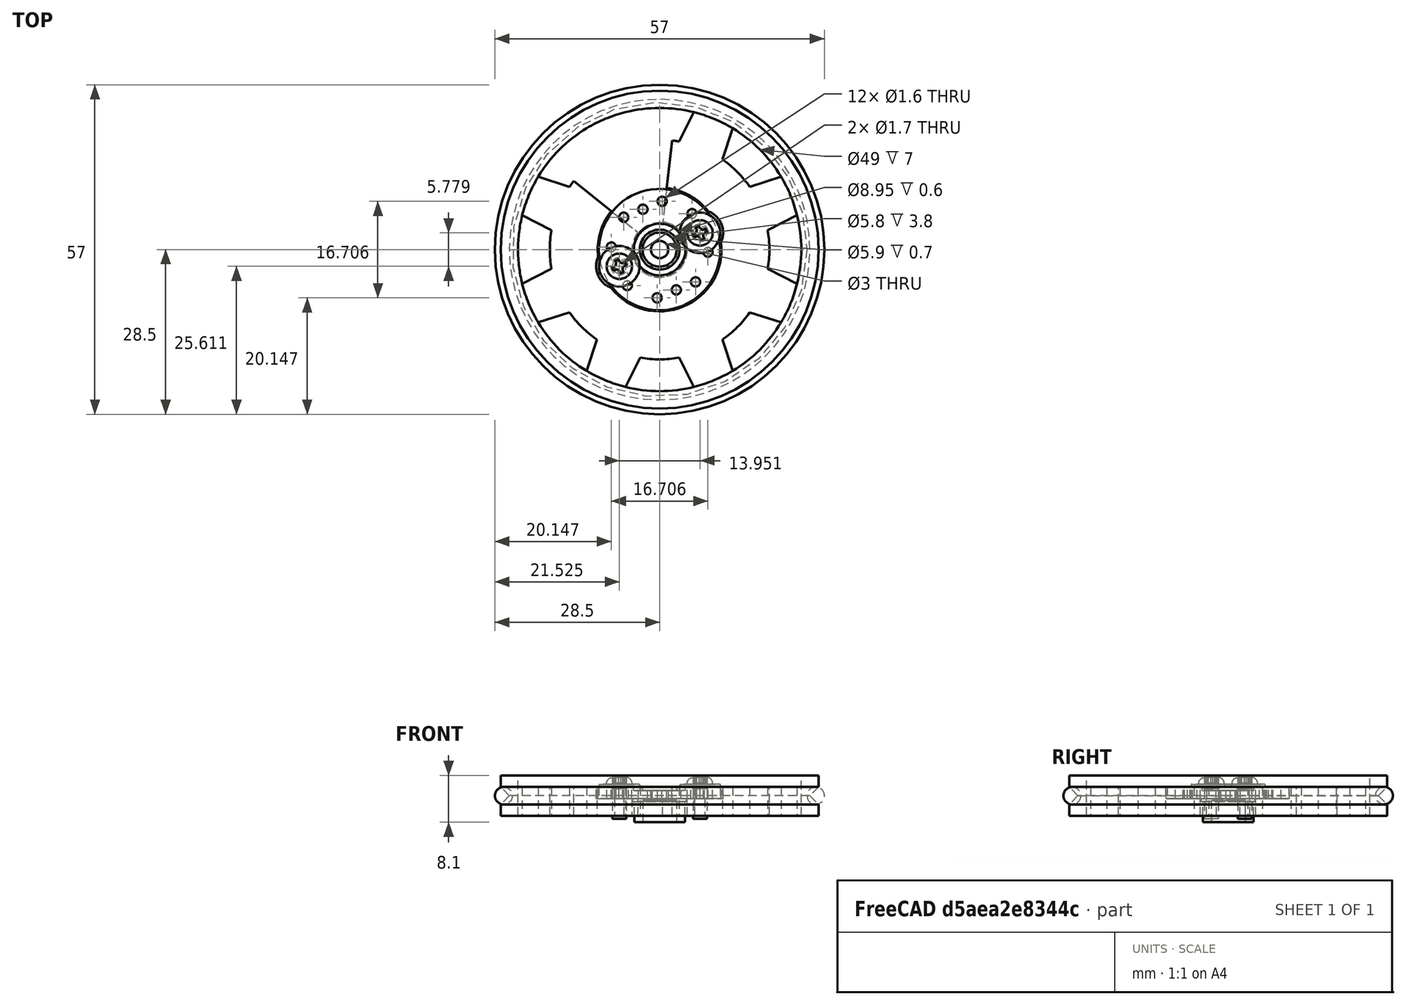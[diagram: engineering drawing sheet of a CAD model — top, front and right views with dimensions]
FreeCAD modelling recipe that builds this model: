
FCSTD DOCUMENT  (FreeCAD 0.14R3702 (Git))
Label: Renacuajo-wheel-open-hardware-assembly
License: CC-BY 3.0
LicenseURL: http://creativecommons.org/licenses/by/3.0/
objects: Part::Feature×4, Part::Torus×1, Part::Compound×1
note: 6 computed .brp shape members not serialized (recipe doc carries the construction recipe); baked Part::Feature solids carry a one-line shape summary decoded from their .brp

FEATURE [Part::Feature] Pocket  label="Renacuajo-open-hardware-wheel"
  Placement = pos=(0,0,0) rot=(1,0,0;1.5708rad)
  shape: bbox 55 x 55 x 7 mm, 43 faces (baked)
FEATURE [Part::Torus] Torus  label="o-ring"
  Angle1 = -180
  Angle2 = 180
  Angle3 = 360
  Radius1 = 27
  Radius2 = 1.5
FEATURE [Part::Feature] Pocket001  label="small-rounded-horn"
  Placement = pos=(0,0,-0.5) rot=(0,0,1;0.392699rad)
  shape: bbox 21 x 21 x 6.2 mm, 28 faces (baked)
FEATURE [Part::Feature] Chamfer  label="screw2"
  Placement = pos=(-6.97529,-2.88926,1.5) rot=(0,0,1;0.392699rad)
  shape: bbox 7 x 7 x 7.14 mm, 33 faces (baked)
FEATURE [Part::Feature] Chamfer001  label="screw1"
  Placement = pos=(6.97529,2.88926,1.5) rot=(0,0,1;0.392699rad)
  shape: bbox 7 x 7 x 7.14 mm, 33 faces (baked)
FEATURE [Part::Compound] Compound  label="Renacuajo-open-hardware-wheel-assembly"
  Links = -> [Pocket,Torus,Pocket001,Chamfer,Chamfer001]
